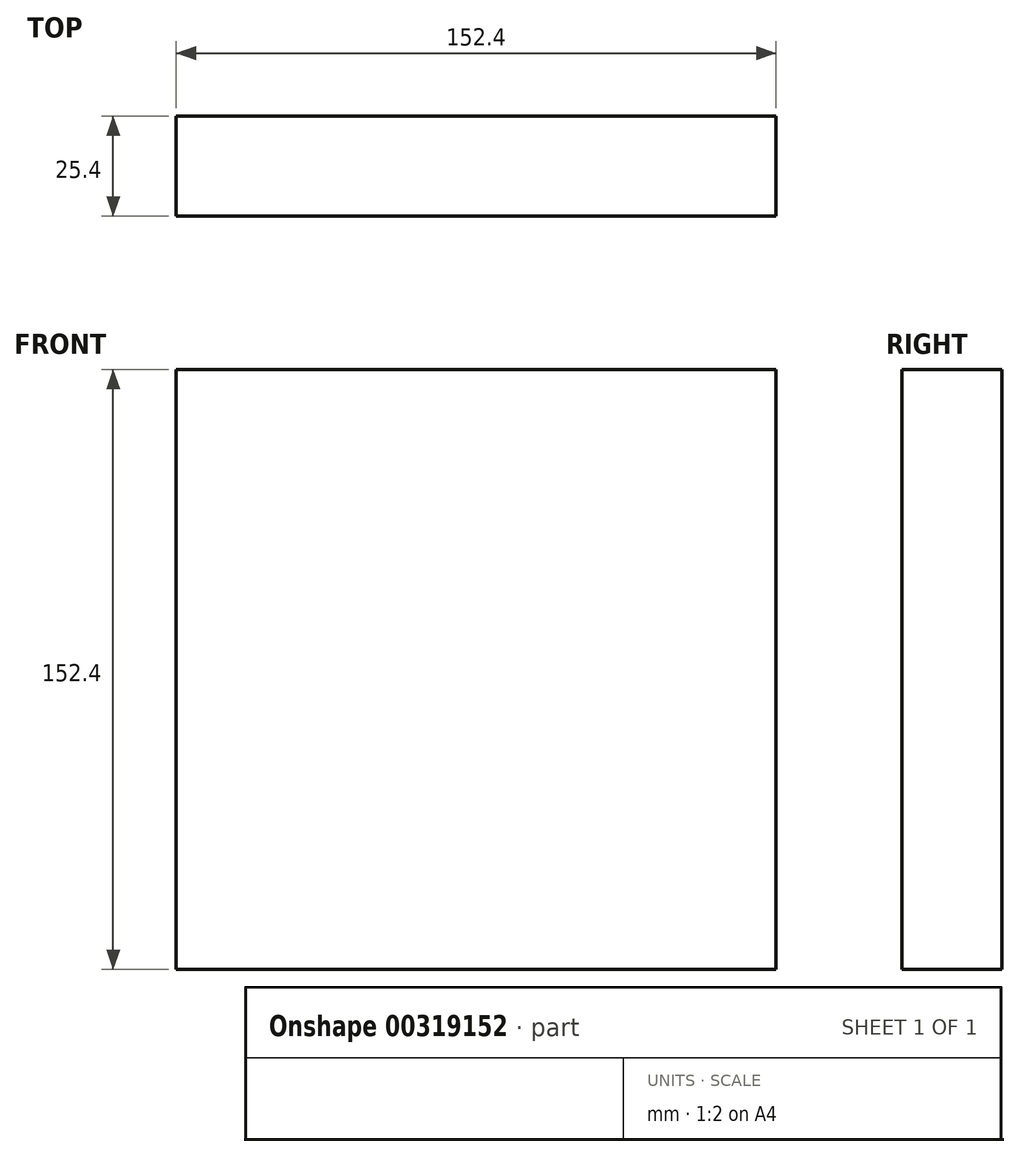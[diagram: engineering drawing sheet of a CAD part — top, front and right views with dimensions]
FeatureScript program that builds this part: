
annotation { "Feature Type Name" : "Feature", "Feature Type Description" : "" }
export const myFeature = defineFeature(function(context is Context, id is Id, definition is map)
    precondition{}
    {
        {
            var Q0;
            Q0=qCreatedBy(makeId("Front.planeOp"),FACE);
            var sketch = newSketch(context, id + "F0", { "sketchPlane" : qUnion([Q0])});
            skLineSegment(sketch, "E0.bottom", {"start": v(0, 0) * mm, "end": v(152.4, 0) * mm});
            skLineSegment(sketch, "E0.top", {"start": v(0, 152.4) * mm, "end": v(152.4, 152.4) * mm});
            skLineSegment(sketch, "E0.left", {"start": v(0, 0) * mm, "end": v(0, 152.4) * mm});
            skLineSegment(sketch, "E0.right", {"start": v(152.4, 0) * mm, "end": v(152.4, 152.4) * mm});
            skSolve(sketch);
        }
        {
            var Q0;
            Q0=makeQuery(id+"F0.imprint","IMPRINT",FACE,{"disambiguationData":[TD([[makeQuery(id+"F0.imprint","IMPRINT",EDGE,{"derivedFrom":sQuery(id+"F0.wireOp",EDGE,"E0.bottom")}),1.0]])]});
            extrude(context, id + "F1", {"entities" : qUnion([Q0]), "depth" : 25.4 * mm});
        }
    });
